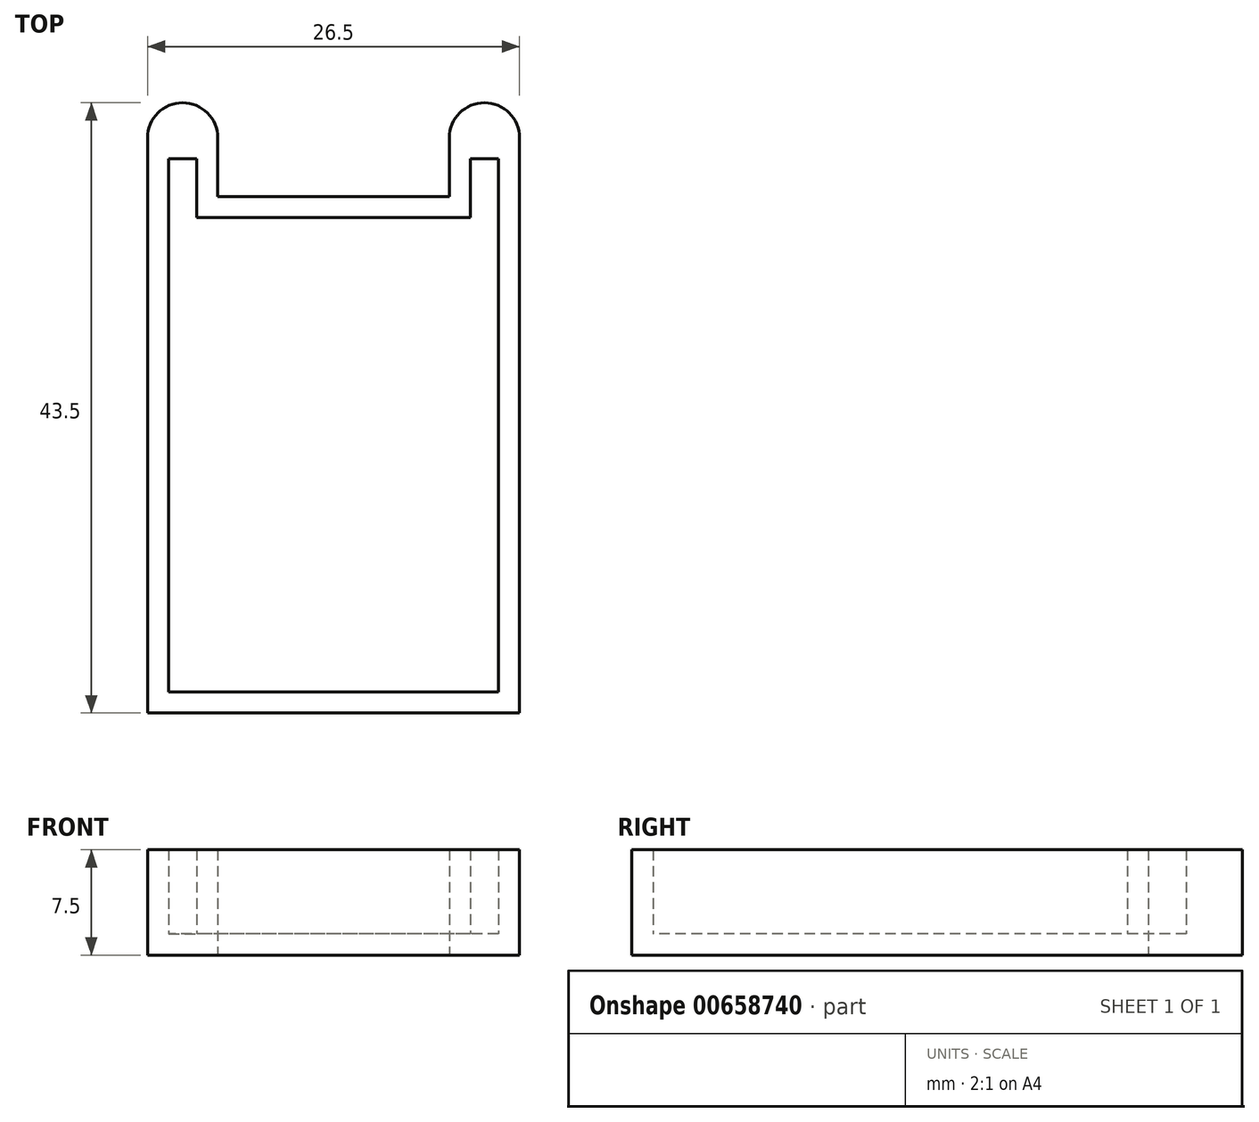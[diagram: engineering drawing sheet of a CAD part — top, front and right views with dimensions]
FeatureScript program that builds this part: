
annotation { "Feature Type Name" : "Feature", "Feature Type Description" : "" }
export const myFeature = defineFeature(function(context is Context, id is Id, definition is map)
    precondition{}
    {
        {
            var Q0;
            Q0=qCreatedBy(makeId("Top.planeOp"),FACE);
            var sketch = newSketch(context, id + "F0", { "sketchPlane" : qUnion([Q0])});
            skLineSegment(sketch, "E0.bottom", {"start": v(9.75, 16.9) * mm, "end": v(-9.75, 16.9) * mm});
            skLineSegment(sketch, "E0.top", {"start": v(11.75, -16.9) * mm, "end": v(-11.75, -16.9) * mm});
            skLineSegment(sketch, "E0.left", {"start": v(11.75, 16.9) * mm, "end": v(11.75, -16.9) * mm});
            skLineSegment(sketch, "E0.right", {"start": v(-11.75, 16.9) * mm, "end": v(-11.75, -16.9) * mm});
            skPoint(sketch, "E0.middle", {"position": v(0, 0) * mm});
            skLineSegment(sketch, "E1.1", {"start": v(13.25, 18.4) * mm, "end": v(13.25, -18.4) * mm});
            skLineSegment(sketch, "E1.2", {"start": v(13.25, -18.4) * mm, "end": v(-13.25, -18.4) * mm});
            skLineSegment(sketch, "E1.3", {"start": v(-13.25, 18.4) * mm, "end": v(-13.25, -18.4) * mm});
            skLineSegment(sketch, "E2", {"start": v(-11.75, 18.4) * mm, "end": v(-11.75, 21.1) * mm});
            skLineSegment(sketch, "E3", {"start": v(-11.75, 21.1) * mm, "end": v(-9.75, 21.1) * mm});
            skLineSegment(sketch, "E4", {"start": v(-9.75, 21.1) * mm, "end": v(-9.75, 18.4) * mm});
            skLineSegment(sketch, "E5", {"start": v(11.75, 18.4) * mm, "end": v(11.75, 21.1) * mm});
            skLineSegment(sketch, "E6", {"start": v(11.75, 21.1) * mm, "end": v(9.75, 21.1) * mm});
            skLineSegment(sketch, "E7", {"start": v(9.75, 21.1) * mm, "end": v(9.75, 18.4) * mm});
            skLineSegment(sketch, "E8.trimOffspring", {"start": v(8.25, 18.4) * mm, "end": v(-8.25, 18.4) * mm});
            skLineSegment(sketch, "E9", {"start": v(-11.75, 16.9) * mm, "end": v(-11.75, 18.4) * mm});
            skLineSegment(sketch, "E10", {"start": v(-9.75, 18.4) * mm, "end": v(-9.75, 16.9) * mm});
            skLineSegment(sketch, "E11", {"start": v(9.75, 18.4) * mm, "end": v(9.75, 16.9) * mm});
            skLineSegment(sketch, "E12", {"start": v(11.75, 16.9) * mm, "end": v(11.75, 18.4) * mm});
            skLineSegment(sketch, "E13.0", {"start": v(-8.25, 22.6) * mm, "end": v(-8.25, 18.4) * mm});
            skLineSegment(sketch, "E13.1", {"start": v(-13.25, 22.6) * mm, "end": v(-8.25, 22.6) * mm});
            skLineSegment(sketch, "E13.2", {"start": v(-13.25, 18.4) * mm, "end": v(-13.25, 22.6) * mm});
            skLineSegment(sketch, "E14.0", {"start": v(8.25, 22.6) * mm, "end": v(8.25, 18.4) * mm});
            skLineSegment(sketch, "E14.1", {"start": v(13.25, 22.6) * mm, "end": v(8.25, 22.6) * mm});
            skLineSegment(sketch, "E14.2", {"start": v(13.25, 18.4) * mm, "end": v(13.25, 22.6) * mm});
            skArc(sketch, "E15", {"start": v(-8.25, 22.6) * mm, "mid": v(-10.75, 25.1) * mm, "end": v(-13.25, 22.6) * mm});
            skArc(sketch, "E16", {"start": v(13.25, 22.6) * mm, "mid": v(10.75, 25.1) * mm, "end": v(8.25, 22.6) * mm});
            skSolve(sketch);
        }
        {
            var Q0;
            Q0=makeQuery(id+"F0.imprint","IMPRINT",FACE,{"disambiguationData":[TD([[makeQuery(id+"F0.imprint","IMPRINT",EDGE,{"derivedFrom":sQuery(id+"F0.wireOp",EDGE,"E0.bottom")}),1.0]])]});
            extrude(context, id + "F1", {"entities" : qUnion([Q0]), "depth" : 1.5 * mm, "offsetDistance" : 25 * mm});
        }
        {
            var Q0;
            Q0 = qSketchRegion(id + "F0", true);
            extrude(context, id + "F2", {"entities" : qUnion([Q0]), "operationType" : NewBodyOperationType.ADD, "depth" : 7.5 * mm, "offsetDistance" : 25 * mm});
        }
    });
